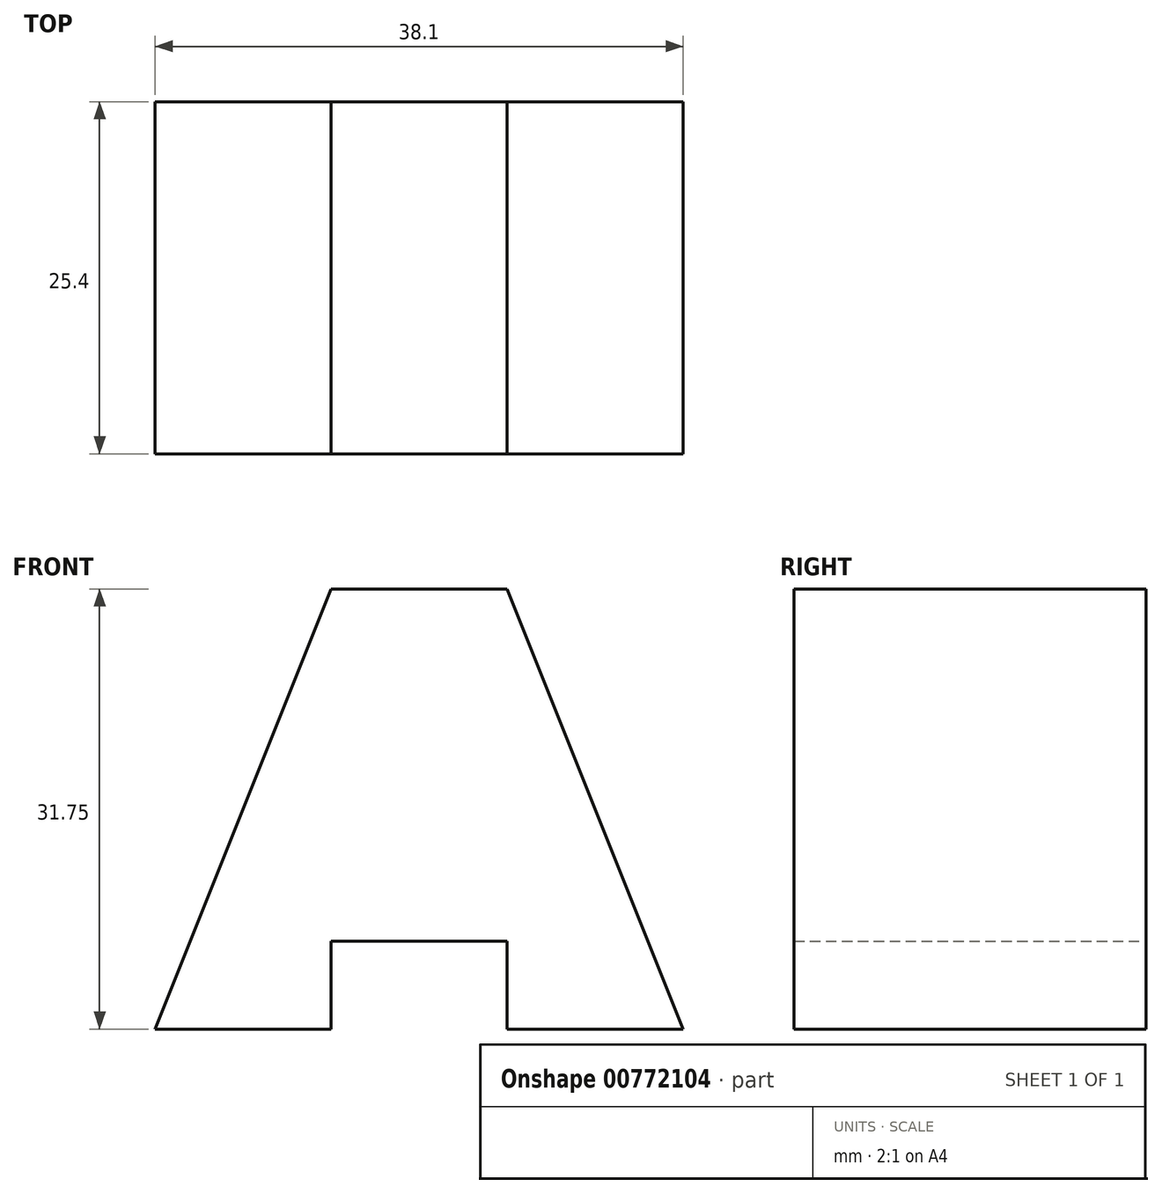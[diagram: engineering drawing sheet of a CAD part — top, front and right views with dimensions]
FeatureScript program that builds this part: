
annotation { "Feature Type Name" : "Feature", "Feature Type Description" : "" }
export const myFeature = defineFeature(function(context is Context, id is Id, definition is map)
    precondition{}
    {
        {
            var Q0;
            Q0=qCreatedBy(makeId("Front.planeOp"),FACE);
            var sketch = newSketch(context, id + "F0", { "sketchPlane" : qUnion([Q0])});
            skLineSegment(sketch, "E0", {"start": v(0, 0) * mm, "end": v(12.7, 0) * mm});
            skLineSegment(sketch, "E1", {"start": v(12.7, 0) * mm, "end": v(12.7, 6.35) * mm});
            skLineSegment(sketch, "E2", {"start": v(12.7, 6.35) * mm, "end": v(25.4, 6.35) * mm});
            skLineSegment(sketch, "E3", {"start": v(25.4, 6.35) * mm, "end": v(25.4, 0) * mm});
            skLineSegment(sketch, "E4", {"start": v(25.4, 0) * mm, "end": v(38.1, 0) * mm});
            skLineSegment(sketch, "E5", {"start": v(25.4, 31.75) * mm, "end": v(12.7, 31.75) * mm});
            skLineSegment(sketch, "E6", {"start": v(0, 0) * mm, "end": v(12.7, 31.75) * mm});
            skLineSegment(sketch, "E7", {"start": v(25.4, 31.75) * mm, "end": v(38.1, 0) * mm});
            skSolve(sketch);
        }
        {
            var Q0;
            Q0=makeQuery(id+"F0.imprint","IMPRINT",FACE,{"disambiguationData":[TD([[makeQuery(id+"F0.imprint","IMPRINT",EDGE,{"derivedFrom":sQuery(id+"F0.wireOp",EDGE,"E0")}),1.0]])]});
            extrude(context, id + "F1", {"entities" : qUnion([Q0]), "depth" : 25.4 * mm, "offsetDistance" : 25.4 * mm});
        }
    });
